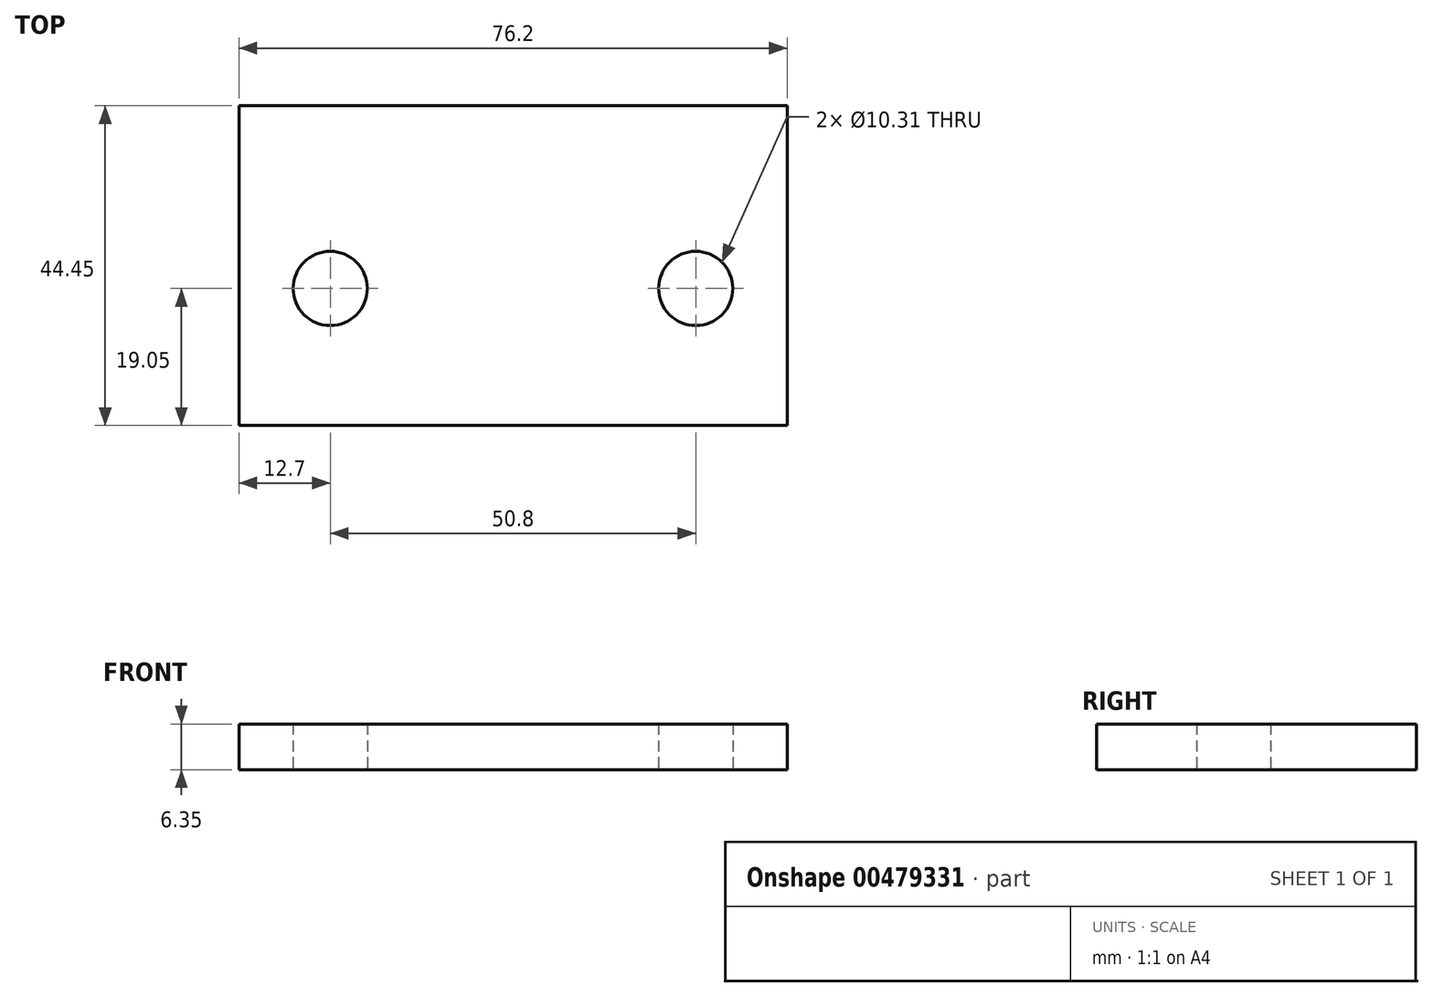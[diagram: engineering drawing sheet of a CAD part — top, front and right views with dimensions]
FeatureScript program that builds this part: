
annotation { "Feature Type Name" : "Feature", "Feature Type Description" : "" }
export const myFeature = defineFeature(function(context is Context, id is Id, definition is map)
    precondition{}
    {
        {
            var Q0;
            Q0=qCreatedBy(makeId("Top.planeOp"),FACE);
            var sketch = newSketch(context, id + "F0", { "sketchPlane" : qUnion([Q0])});
            skLineSegment(sketch, "E0.bottom", {"start": v(0, 0) * mm, "end": v(76.2, 0) * mm});
            skLineSegment(sketch, "E0.top", {"start": v(0, -44.45) * mm, "end": v(76.2, -44.45) * mm});
            skLineSegment(sketch, "E0.left", {"start": v(0, 0) * mm, "end": v(0, -44.45) * mm});
            skLineSegment(sketch, "E0.right", {"start": v(76.2, 0) * mm, "end": v(76.2, -44.45) * mm});
            skCircle(sketch, "E1", {"center": v(12.7, -25.4) * mm, "radius": 5.16 * mm});
            skCircle(sketch, "E2.MirrorC", {"center": v(63.5, -25.4) * mm, "radius": 5.16 * mm});
            skSolve(sketch);
        }
        {
            var Q0;
            Q0=makeQuery(id+"F0.imprint","IMPRINT",FACE,{"disambiguationData":[TD([[makeQuery(id+"F0.imprint","IMPRINT",EDGE,{"derivedFrom":sQuery(id+"F0.wireOp",EDGE,"E0.bottom")}),-1.0]])]});
            extrude(context, id + "F1", {"entities" : qUnion([Q0]), "depth" : 6.35 * mm});
        }
    });
